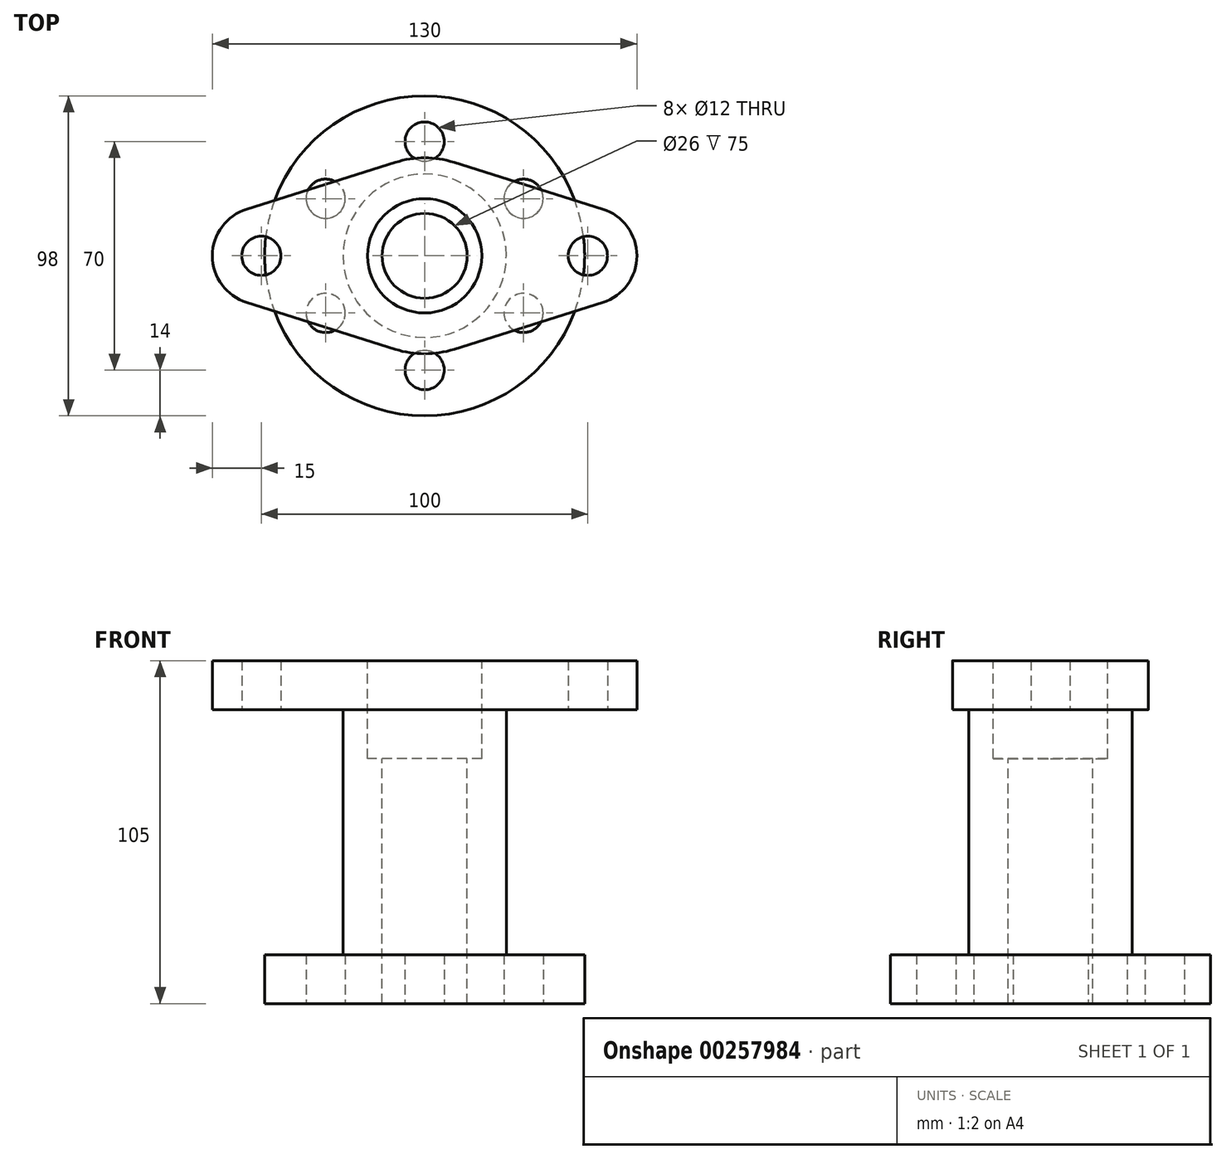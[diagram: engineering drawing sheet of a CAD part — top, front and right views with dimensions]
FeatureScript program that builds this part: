
annotation { "Feature Type Name" : "Feature", "Feature Type Description" : "" }
export const myFeature = defineFeature(function(context is Context, id is Id, definition is map)
    precondition{}
    {
        {
            var Q0;
            Q0=qCreatedBy(makeId("Top.planeOp"),FACE);
            var sketch = newSketch(context, id + "F0", { "sketchPlane" : qUnion([Q0])});
            skCircle(sketch, "E0", {"center": v(0, 0) * mm, "radius": 49 * mm});
            skCircle(sketch, "E1", {"center": v(0, 35) * mm, "radius": 6 * mm});
            skCircle(sketch, "E2.1.0", {"center": v(-30.31, 17.5) * mm, "radius": 6 * mm});
            skCircle(sketch, "E2.2.0", {"center": v(-30.31, -17.5) * mm, "radius": 6 * mm});
            skCircle(sketch, "E2.3.0", {"center": v(0, -35) * mm, "radius": 6 * mm});
            skCircle(sketch, "E2.4.0", {"center": v(30.31, -17.5) * mm, "radius": 6 * mm});
            skCircle(sketch, "E2.5.0", {"center": v(30.31, 17.5) * mm, "radius": 6 * mm});
            skCircle(sketch, "E3", {"center": v(0, 0) * mm, "radius": 35 * mm, "construction": true});
            skSolve(sketch);
        }
        {
            var Q0;
            Q0=makeQuery(id+"F0.imprint","IMPRINT",FACE,{"disambiguationData":[TD([[makeQuery(id+"F0.imprint","IMPRINT",EDGE,{"derivedFrom":sQuery(id+"F0.wireOp",EDGE,"E0")}),1.0]])]});
            extrude(context, id + "F1", {"entities" : qUnion([Q0]), "depth" : 15 * mm});
        }
        {
            var Q0;
            Q0=makeQuery(id+"F1.opExtrude","CAP_FACE",FACE,{"disambiguationData":[OSD([sQuery(id+"F0.wireOp",EDGE,"E0"),sQuery(id+"F0.wireOp",EDGE,"E1"),sQuery(id+"F0.wireOp",EDGE,"E2.1.0"),sQuery(id+"F0.wireOp",EDGE,"E2.2.0"),sQuery(id+"F0.wireOp",EDGE,"E2.3.0"),sQuery(id+"F0.wireOp",EDGE,"E2.4.0"),sQuery(id+"F0.wireOp",EDGE,"E2.5.0")])],"isStart":false});
            var sketch = newSketch(context, id + "F2", { "sketchPlane" : qUnion([Q0])});
            skCircle(sketch, "E4", {"center": v(0, 0) * mm, "radius": 25.02 * mm});
            skSolve(sketch);
        }
        {
            var Q0;
            Q0 = qSketchRegion(id + "F2", true);
            extrude(context, id + "F3", {"entities" : qUnion([Q0]), "operationType" : NewBodyOperationType.ADD, "depth" : 75 * mm});
        }
        {
            var Q0;
            Q0=makeQuery(id+"F3.opExtrude","CAP_FACE",FACE,{"disambiguationData":[OSD([sQuery(id+"F2.wireOp",EDGE,"E4")])],"isStart":false});
            var sketch = newSketch(context, id + "F4", { "sketchPlane" : qUnion([Q0])});
            skCircle(sketch, "E5", {"center": v(-50, 0) * mm, "radius": 6 * mm});
            skArc(sketch, "E6", {"start": v(54.5, -14.3) * mm, "mid": v(65, 0) * mm, "end": v(54.5, 14.3) * mm});
            skCircle(sketch, "E7", {"center": v(50, 0) * mm, "radius": 6 * mm});
            skLineSegment(sketch, "E8", {"start": v(-54.5, 14.3) * mm, "end": v(-8.41, 28.8) * mm});
            skLineSegment(sketch, "E9", {"start": v(8.41, 28.8) * mm, "end": v(54.5, 14.3) * mm});
            skLineSegment(sketch, "E10", {"start": v(54.5, -14.3) * mm, "end": v(8.41, -28.8) * mm});
            skArc(sketch, "E11", {"start": v(-9, -28.62) * mm, "mid": v(0, -30) * mm, "end": v(9, -28.62) * mm});
            skArc(sketch, "E12", {"start": v(-54.5, 14.3) * mm, "mid": v(-65, 0) * mm, "end": v(-54.5, -14.3) * mm});
            skLineSegment(sketch, "E13", {"start": v(-50, 0) * mm, "end": v(50, 0) * mm, "construction": true});
            skLineSegment(sketch, "E14.MirrorCS", {"start": v(-54.5, -14.3) * mm, "end": v(-8.41, -28.8) * mm});
            skArc(sketch, "E15.trimOffspring", {"start": v(9, 28.62) * mm, "mid": v(0, 30) * mm, "end": v(-9, 28.62) * mm});
            skSolve(sketch);
        }
        {
            var Q0;
            Q0 = qSketchRegion(id + "F4", true);
            extrude(context, id + "F5", {"entities" : qUnion([Q0]), "operationType" : NewBodyOperationType.ADD, "depth" : 15 * mm});
        }
        {
            var Q0;
            Q0=makeQuery(id+"F5.opExtrude","CAP_FACE",FACE,{"disambiguationData":[OSD([sQuery(id+"F4.wireOp",EDGE,"cR5ZLbEm-5cvQ-HoFG-hkaR-shYXEnD0GYR8"),sQuery(id+"F4.wireOp",EDGE,"E5"),sQuery(id+"F4.wireOp",EDGE,"fjpzYiwP-HFGl-IrN7-2xlk-wh6lL9XPCbcZ"),sQuery(id+"F4.wireOp",EDGE,"E6"),sQuery(id+"F4.wireOp",EDGE,"E7"),sQuery(id+"F4.wireOp",EDGE,"E8"),sQuery(id+"F4.wireOp",EDGE,"E9"),sQuery(id+"F4.wireOp",EDGE,"E10"),sQuery(id+"F4.wireOp",EDGE,"YojxMDkp-BJkm-TkNb-T44b-luTLRWdy0Y4R"),sQuery(id+"F4.wireOp",EDGE,"b8ddf683-e840-46ba-98d6-28128c06984a.trimOffspring")])],"isStart":false});
            var sketch = newSketch(context, id + "F6", { "sketchPlane" : qUnion([Q0])});
            skCircle(sketch, "E16", {"center": v(0, 0) * mm, "radius": 17.5 * mm});
            skSolve(sketch);
        }
        {
            var Q0;
            Q0 = qSketchRegion(id + "F6", true);
            extrude(context, id + "F7", {"entities" : qUnion([Q0]), "oppositeDirection" : true, "depth" : 30 * mm});
        }
        {
            var Q0;
            Q0=makeQuery(id+"F7.opExtrude","SWEPT_BODY",BODY,{"disambiguationData":[OSD([sQuery(id+"F6.wireOp",EDGE,"E16")])]});
            var Q1;
            Q1=makeQuery(id+"F1.opExtrude","SWEPT_BODY",BODY,{"disambiguationData":[OSD([sQuery(id+"F0.wireOp",EDGE,"E0"),sQuery(id+"F0.wireOp",EDGE,"E1"),sQuery(id+"F0.wireOp",EDGE,"E2.1.0"),sQuery(id+"F0.wireOp",EDGE,"E2.2.0"),sQuery(id+"F0.wireOp",EDGE,"E2.3.0"),sQuery(id+"F0.wireOp",EDGE,"E2.4.0"),sQuery(id+"F0.wireOp",EDGE,"E2.5.0")])]});
            booleanBodies(context, id + "F8", {"operationType" : BooleanOperationType.SUBTRACTION, "tools" : qUnion([Q0]), "targets" : qUnion([Q1])});
        }
        {
            var Q0;
            Q0=makeQuery(id+"F8.opBoolean","COPY",FACE,{"derivedFrom":makeQuery(id+"F7.opExtrude","CAP_FACE",FACE,{"disambiguationData":[OSD([sQuery(id+"F6.wireOp",EDGE,"E16")])],"isStart":false})});
            var sketch = newSketch(context, id + "F9", { "sketchPlane" : qUnion([Q0])});
            skCircle(sketch, "E17", {"center": v(0, 0) * mm, "radius": 13 * mm});
            skSolve(sketch);
        }
        {
            var Q0;
            Q0 = qSketchRegion(id + "F9", true);
            extrude(context, id + "F10", {"entities" : qUnion([Q0]), "oppositeDirection" : true, "depth" : 150 * mm});
        }
        {
            var Q0;
            Q0=makeQuery(id+"F10.opExtrude","SWEPT_BODY",BODY,{"disambiguationData":[OSD([sQuery(id+"F9.wireOp",EDGE,"E17")])]});
            var Q1;
            Q1=makeQuery(id+"F1.opExtrude","SWEPT_BODY",BODY,{"disambiguationData":[OSD([sQuery(id+"F0.wireOp",EDGE,"E0"),sQuery(id+"F0.wireOp",EDGE,"E1"),sQuery(id+"F0.wireOp",EDGE,"E2.1.0"),sQuery(id+"F0.wireOp",EDGE,"E2.2.0"),sQuery(id+"F0.wireOp",EDGE,"E2.3.0"),sQuery(id+"F0.wireOp",EDGE,"E2.4.0"),sQuery(id+"F0.wireOp",EDGE,"E2.5.0")])]});
            booleanBodies(context, id + "F11", {"operationType" : BooleanOperationType.SUBTRACTION, "tools" : qUnion([Q0]), "targets" : qUnion([Q1])});
        }
    });
